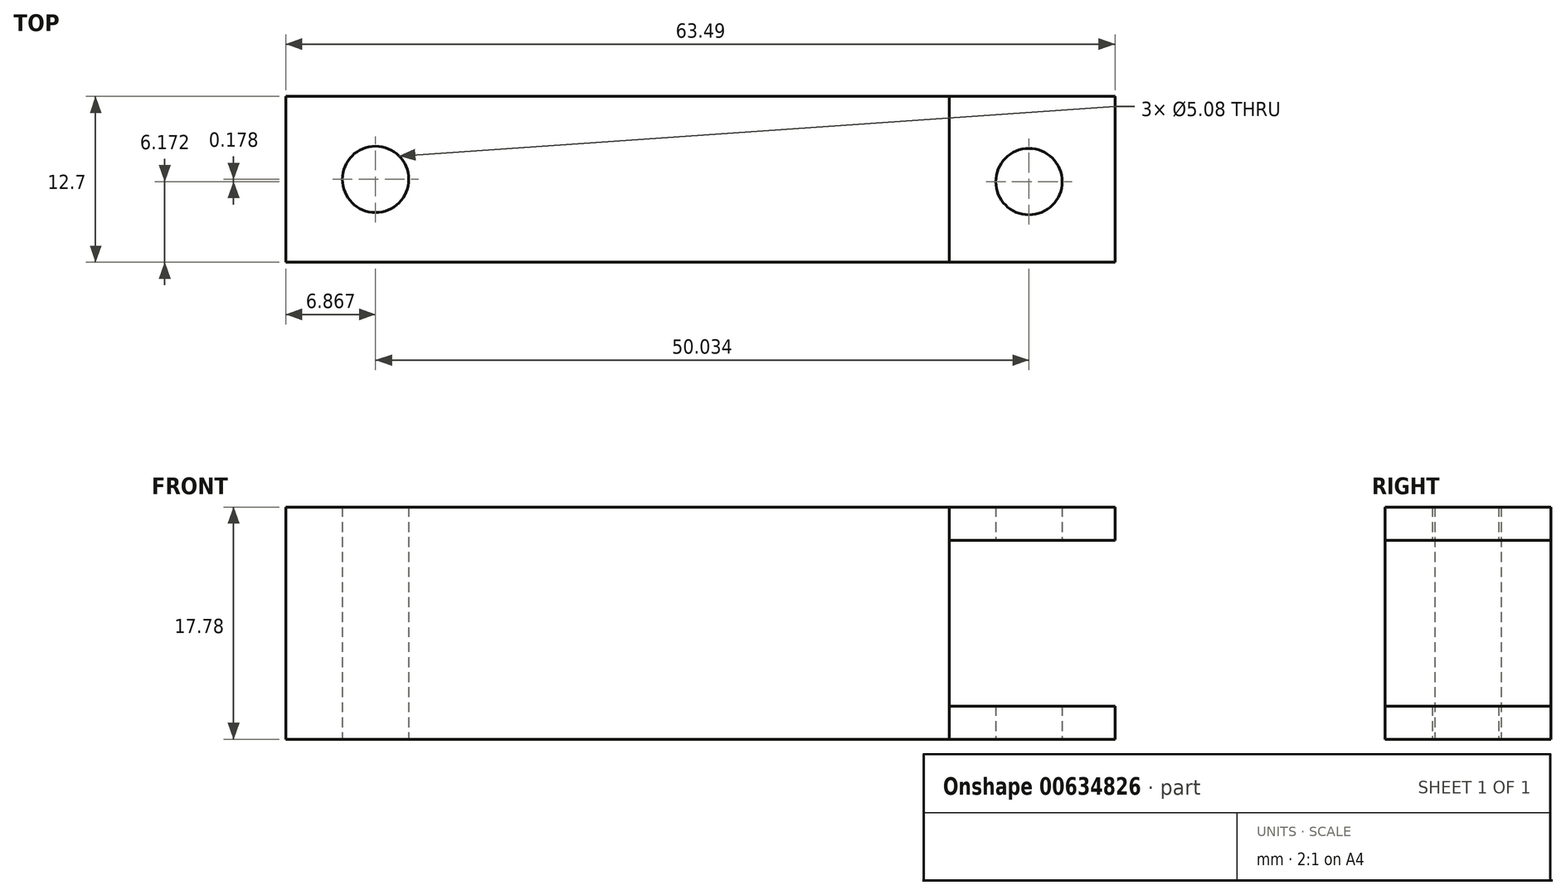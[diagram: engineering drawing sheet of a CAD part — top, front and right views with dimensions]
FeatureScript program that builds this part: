
annotation { "Feature Type Name" : "Feature", "Feature Type Description" : "" }
export const myFeature = defineFeature(function(context is Context, id is Id, definition is map)
    precondition{}
    {
        {
            var Q0;
            Q0=qCreatedBy(makeId("Top.planeOp"),FACE);
            var sketch = newSketch(context, id + "F0", { "sketchPlane" : qUnion([Q0])});
            skLineSegment(sketch, "E0.bottom", {"start": v(25.4, 6.35) * mm, "end": v(-25.4, 6.35) * mm});
            skLineSegment(sketch, "E0.top", {"start": v(25.4, -6.35) * mm, "end": v(-25.4, -6.35) * mm});
            skLineSegment(sketch, "E0.left", {"start": v(25.4, 6.35) * mm, "end": v(25.4, -6.35) * mm});
            skLineSegment(sketch, "E0.right", {"start": v(-25.4, 6.35) * mm, "end": v(-25.4, -6.35) * mm});
            skPoint(sketch, "E0.middle", {"position": v(0, 0) * mm});
            skCircle(sketch, "E1", {"center": v(-18.53, 0) * mm, "radius": 2.54 * mm});
            skSolve(sketch);
        }
        {
            var Q0;
            Q0=makeQuery(id+"F0.imprint","IMPRINT",FACE,{"disambiguationData":[TD([[makeQuery(id+"F0.imprint","IMPRINT",EDGE,{"derivedFrom":sQuery(id+"F0.wireOp",EDGE,"E0.bottom")}),1.0]])]});
            extrude(context, id + "F1", {"entities" : qUnion([Q0]), "endBound" : BoundingType.SYMMETRIC, "depth" : 17.78 * mm, "offsetDistance" : 25.4 * mm});
        }
        {
            var Q0;
            Q0=qCreatedBy(makeId("Top.planeOp"),FACE);
            var sketch = newSketch(context, id + "F2", { "sketchPlane" : qUnion([Q0])});
            skLineSegment(sketch, "E2.bottom", {"start": v(26.66, 6.52) * mm, "end": v(39.36, 6.52) * mm});
            skLineSegment(sketch, "E2.top", {"start": v(26.66, -6.18) * mm, "end": v(39.36, -6.18) * mm});
            skLineSegment(sketch, "E2.left", {"start": v(26.66, 6.52) * mm, "end": v(26.66, -6.18) * mm});
            skLineSegment(sketch, "E2.right", {"start": v(39.36, 6.52) * mm, "end": v(39.36, -6.18) * mm});
            skCircle(sketch, "E3", {"center": v(32.77, 0) * mm, "radius": 2.54 * mm});
            skSolve(sketch);
        }
        {
            var Q0;
            Q0=makeQuery(id+"F2.imprint","IMPRINT",FACE,{"disambiguationData":[TD([[makeQuery(id+"F2.imprint","IMPRINT",EDGE,{"derivedFrom":sQuery(id+"F2.wireOp",EDGE,"E2.bottom")}),-1.0]])]});
            extrude(context, id + "F3", {"entities" : qUnion([Q0]), "endBound" : BoundingType.SYMMETRIC, "depth" : 2.54 * mm, "offsetDistance" : 25.4 * mm});
        }
        {
            var Q0;
            Q0=makeQuery(id+"F3.opExtrude","SWEPT_BODY",BODY,{"disambiguationData":[OSD([sQuery(id+"F2.wireOp",EDGE,"E2.bottom"),sQuery(id+"F2.wireOp",EDGE,"E2.top"),sQuery(id+"F2.wireOp",EDGE,"E2.left"),sQuery(id+"F2.wireOp",EDGE,"E2.right"),sQuery(id+"F2.wireOp",EDGE,"E3")])]});
            transform(context, id + "F4", {"entities" : qUnion([Q0]), "transformType" : TransformType.TRANSLATION_3D, "dx" : -1.27 * mm, "dy" : -0.18 * mm, "dz" : 7.62 * mm, "makeCopy" : true});
        }
        {
            var Q0;
            Q0=makeQuery(id+"F3.opExtrude","SWEPT_BODY",BODY,{"disambiguationData":[OSD([sQuery(id+"F2.wireOp",EDGE,"E2.bottom"),sQuery(id+"F2.wireOp",EDGE,"E2.top"),sQuery(id+"F2.wireOp",EDGE,"E2.left"),sQuery(id+"F2.wireOp",EDGE,"E2.right"),sQuery(id+"F2.wireOp",EDGE,"E3")])]});
            deleteBodies(context, id + "F5", {"entities" : qUnion([Q0])});
        }
        {
            var Q0;
            Q0=makeQuery(id+"F4.opPattern","COPY",BODY,{"derivedFrom":makeQuery(id+"F3.opExtrude","SWEPT_BODY",BODY,{"disambiguationData":[OSD([sQuery(id+"F2.wireOp",EDGE,"E2.bottom"),sQuery(id+"F2.wireOp",EDGE,"E2.top"),sQuery(id+"F2.wireOp",EDGE,"E2.left"),sQuery(id+"F2.wireOp",EDGE,"E2.right"),sQuery(id+"F2.wireOp",EDGE,"E3")])]}),"instanceName":"1"});
            transform(context, id + "F6", {"entities" : qUnion([Q0]), "transformType" : TransformType.TRANSLATION_3D, "dx" : 0 * mm, "dy" : 0 * mm, "dz" : -15.24 * mm, "makeCopy" : true});
        }
    });
